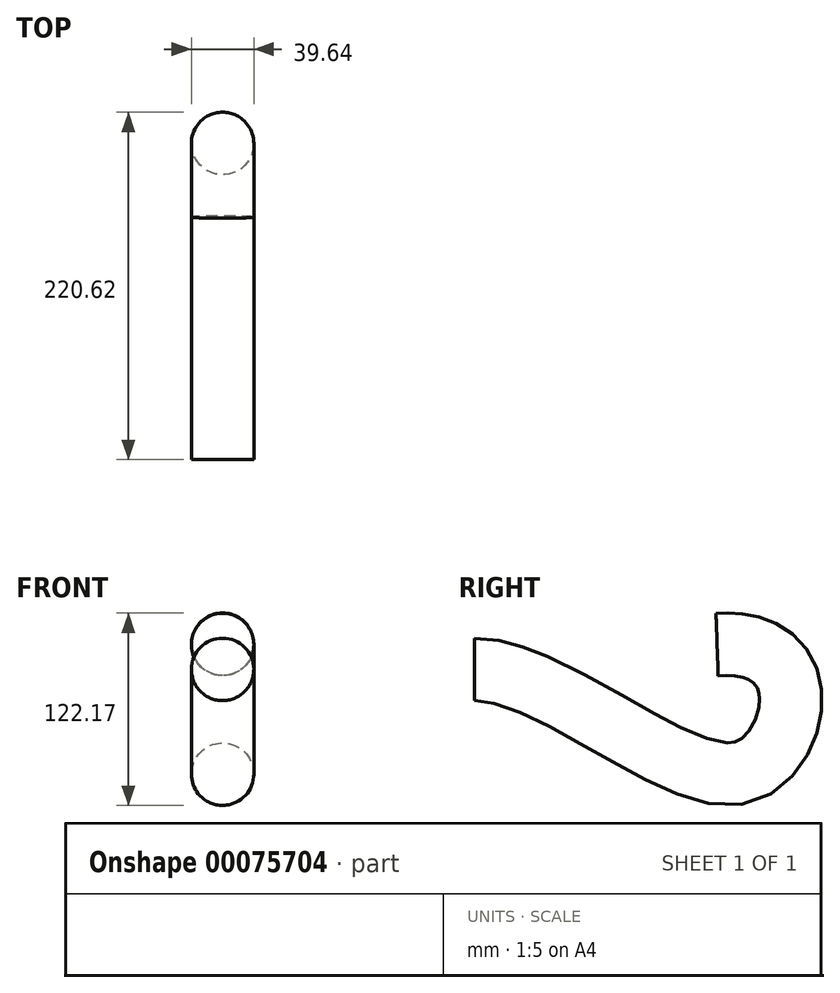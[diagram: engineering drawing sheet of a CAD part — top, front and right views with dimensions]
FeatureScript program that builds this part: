
annotation { "Feature Type Name" : "Feature", "Feature Type Description" : "" }
export const myFeature = defineFeature(function(context is Context, id is Id, definition is map)
    precondition{}
    {
        {
            var Q0;
            Q0=qCreatedBy(makeId("Front.planeOp"),FACE);
            var sketch = newSketch(context, id + "F0", { "sketchPlane" : qUnion([Q0])});
            skCircle(sketch, "E0", {"center": v(0, 0) * mm, "radius": 19.82 * mm});
            skLineSegment(sketch, "E1.rect.bottom", {"start": v(-25.97, 38.8) * mm, "end": v(25.97, 38.8) * mm});
            skLineSegment(sketch, "E1.rect.top", {"start": v(-25.97, -38.8) * mm, "end": v(25.97, -38.8) * mm});
            skLineSegment(sketch, "E1.rect.left", {"start": v(-25.97, 38.8) * mm, "end": v(-25.97, -38.8) * mm});
            skLineSegment(sketch, "E1.rect.right", {"start": v(25.97, 38.8) * mm, "end": v(25.97, -38.8) * mm});
            skSolve(sketch);
        }
        {
            var Q0;
            Q0=qCreatedBy(makeId("Right.planeOp"),FACE);
            var sketch = newSketch(context, id + "F1", { "sketchPlane" : qUnion([Q0])});
            skFitSpline(sketch, "E2", {"points": [v(0, 0) * mm, v(159.14, -66.48) * mm, v(198.5, -33.72) * mm, v(195.63, 0) * mm, v(174.8, 14.4) * mm, v(153.98, 15.83) * mm], "startDerivative": vector(377.52, 0) * mm, "endDerivative": vector(-160.92, -5.56) * mm});
            skSolve(sketch);
        }
        {
            var Q0;
            Q0=makeQuery(id+"F0.imprint","IMPRINT",FACE,{"disambiguationData":[TD([[makeQuery(id+"F0.imprint","IMPRINT",EDGE,{"derivedFrom":sQuery(id+"F0.wireOp",EDGE,"E0")}),1.0]])]});
            var Q1;
            Q1=sQuery(id+"F1.wireOp",EDGE,"E2");
            sweep(context, id + "F2", {"profiles" : qUnion([Q0]), "path" : qUnion([Q1])});
        }
    });
